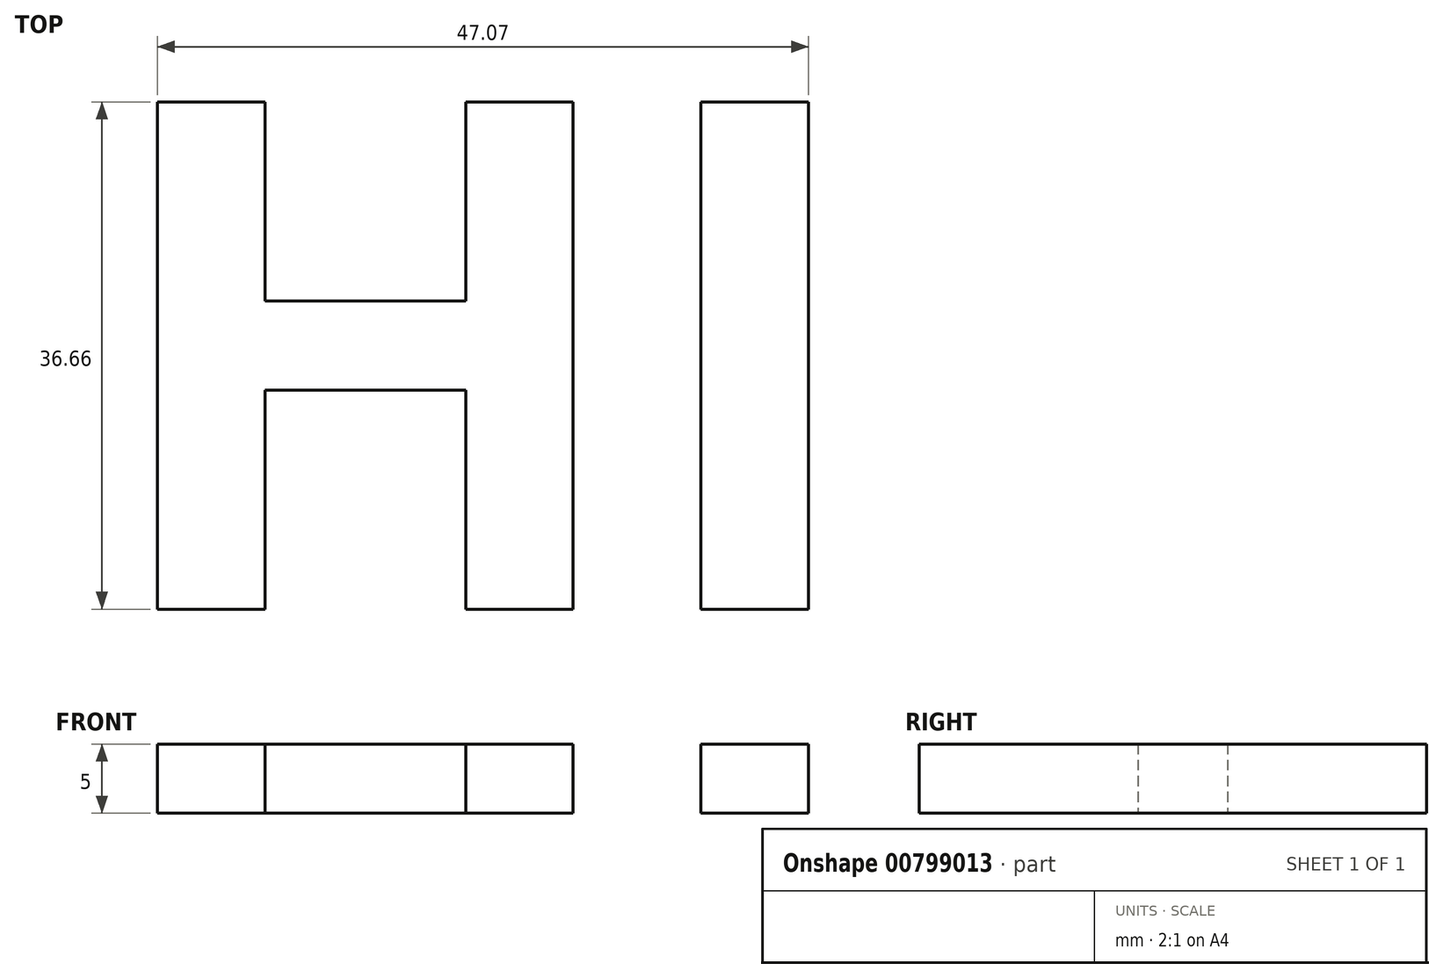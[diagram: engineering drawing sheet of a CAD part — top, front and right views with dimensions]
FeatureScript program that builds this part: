
annotation { "Feature Type Name" : "Feature", "Feature Type Description" : "" }
export const myFeature = defineFeature(function(context is Context, id is Id, definition is map)
    precondition{}
    {
        {
            var Q0;
            Q0=qCreatedBy(makeId("Top.planeOp"),FACE);
            var sketch = newSketch(context, id + "F0", { "sketchPlane" : qUnion([Q0])});
            skLineSegment(sketch, "E0.bottom", {"start": v(31.5, -18.5) * mm, "end": v(-31.5, -18.5) * mm});
            skLineSegment(sketch, "E0.top", {"start": v(31.5, 18.5) * mm, "end": v(-31.5, 18.5) * mm});
            skLineSegment(sketch, "E0.left", {"start": v(31.5, -18.5) * mm, "end": v(31.5, 18.5) * mm});
            skLineSegment(sketch, "E0.right", {"start": v(-31.5, -18.5) * mm, "end": v(-31.5, 18.5) * mm});
            skPoint(sketch, "E0.middle", {"position": v(0, 0) * mm});
            skSolve(sketch);
        }
        {
            var Q0;
            Q0=qCreatedBy(makeId("Top.planeOp"),FACE);
            var sketch = newSketch(context, id + "F1", { "sketchPlane" : qUnion([Q0])});
            skText(sketch, "E1", { "text": "HI", "fontName": "OpenSans-Bold.ttf"});
            const initialGuessF1  = {"E1": [-0.0275, -0.0182, 1, 0, 0.03697]};
            skSetInitialGuess(sketch, initialGuessF1);
            skSolve(sketch);
        }
        {
            var Q0;
            Q0 = qSketchRegion(id + "F1", true);
            extrude(context, id + "F2", {"entities" : qUnion([Q0]), "depth" : 5 * mm, "offsetDistance" : 25 * mm});
        }
    });
